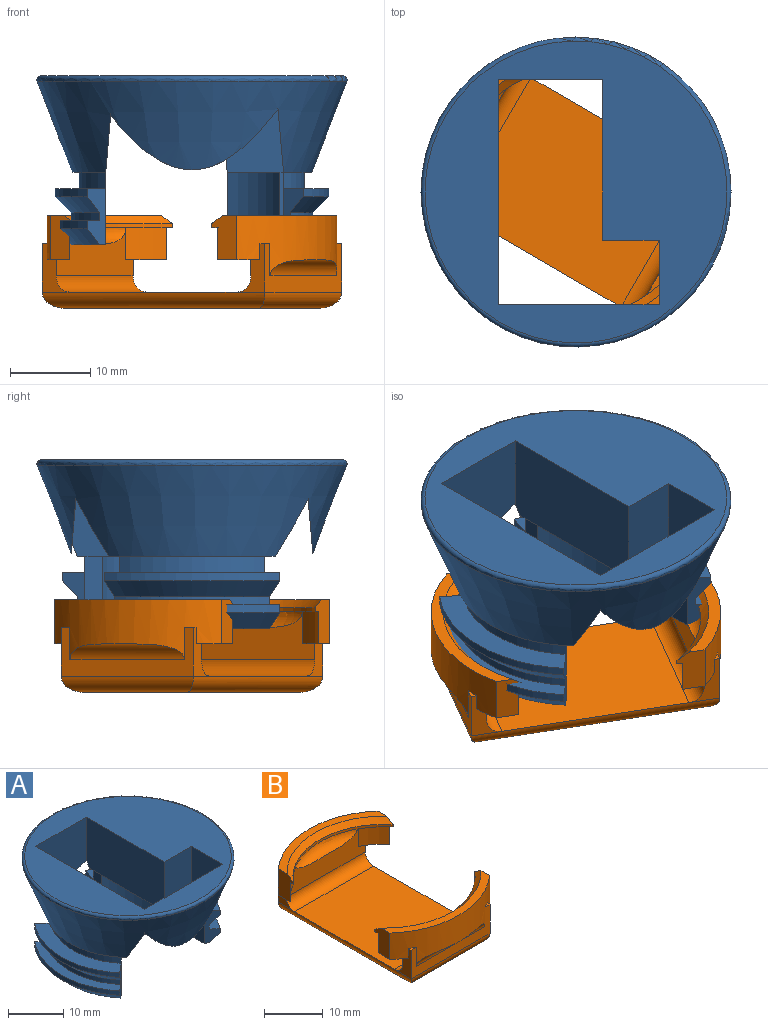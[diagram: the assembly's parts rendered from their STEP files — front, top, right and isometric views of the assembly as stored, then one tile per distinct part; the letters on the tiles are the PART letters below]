
ASSEMBLY  parts=2 mates=1
PART A: 42 faces, bbox 41.7x41.7x21 mm
  f0: cylinder r=15mm len=22.99mm, axis (0,0,1), area 28.1mm2, adj f25,f27,f32,f39
  f1: cylinder r=15mm len=19.28mm, axis (0,0,1), area 20.9mm2, adj f29,f30,f33,f37
  f2: plane 10.77x1.28mm, normal (0,0,-1), area 9.3mm2, adj f7,f23
  f3: plane 16.12x7.63mm, normal (0,0,-1), area 97.8mm2, adj f9,f10,f19
  f4: cone r=19.5mm half-angle=21deg, axis (0,0,1), area 1180.5mm2, adj f5,f6,f7,f8,f9,f11,f12,f14
  f5: plane 23.85x10.52mm, normal (0,0,-1), area 24.9mm2, adj f4,f9,f11,f16
  f6: plane 20.81x11.67mm, normal (0,1,-0.09), area 190.7mm2, adj f4,f7,f11,f13
  f7: plane 28.86x12mm, normal (1,0,-0.09), area 317.3mm2, adj f2,f4,f6,f8,f12,f13,f20,f22
  f8: plane 14.36x11.68mm, normal (0,-1,-0.09), area 136.9mm2, adj f4,f7,f9,f13
  f9: plane 20.92x12.01mm, normal (-1,0,-0.09), area 240.3mm2, adj f3,f4,f5,f8,f10,f13,f15
  f10: plane 12x8.05mm, normal (0,-1,-0.09), area 84.3mm2, adj f3,f9,f11,f13,f18
  f11: plane 12x9.42mm, normal (-1,0,-0.09), area 88.4mm2, adj f4,f5,f6,f10,f13,f17
  f12: plane 20.67x4.17mm, normal (0,0,-1), area 19mm2, adj f4,f7,f21
  f13: plane 37.52x37.52mm, normal (0,0,1), area 685.7mm2, adj f6,f7,f8,f9,f10,f11,f14
  f14: torus R=18.76mm, axis (0,0,1), area 118.2mm2, adj f4,f13
  f15: plane 9x2.12mm, normal (-1,0,0), area 19.1mm2, adj f9,f16,f19,f25,f35
  f16: cylinder r=14mm len=21.46mm, axis (0,0,1), area 52.5mm2, adj f5,f15,f17,f24
  f17: plane 9x3.21mm, normal (-1,0,0), area 28.9mm2, adj f11,f16,f18,f27,f35
  f18: plane 9x0.44mm, normal (0,-1,0), area 4mm2, adj f10,f17,f19,f35
  f19: cylinder r=12mm len=16.12mm, axis (0,0,1), area 175.3mm2, adj f3,f15,f18,f35
  f20: plane 9x3.62mm, normal (1,0,0), area 32.5mm2, adj f7,f21,f23,f30,f34
  f21: cylinder r=14mm len=18mm, axis (0,0,1), area 39.1mm2, adj f12,f20,f22,f28
  f22: plane 9x3.62mm, normal (1,0,0), area 32.5mm2, adj f7,f21,f23,f29,f34
  f23: cylinder r=12mm len=10.77mm, axis (0,0,1), area 100.5mm2, adj f2,f20,f22,f34
  f24: plane 26.06x12.63mm, normal (0,0,1), area 87.2mm2, adj f16,f25,f26,f27
  f25: plane 7x2.85mm, normal (-0.95,0.31,0), area 15mm2, adj f0,f15,f24,f26,f32,f35,f38,f39
  f26: cylinder r=17mm len=26.06mm, axis (0,0,1), area 31.9mm2, adj f24,f25,f27,f32
  f27: plane 7x2.44mm, normal (-0.58,-0.81,0), area 15mm2, adj f0,f17,f24,f26,f32,f35,f38,f39
  f28: plane 21.85x6.28mm, normal (0,0,1), area 64.9mm2, adj f21,f29,f30,f31
  f29: plane 7x2.3mm, normal (0.64,0.77,0), area 15mm2, adj f1,f22,f28,f31,f33,f34,f36,f37
  f30: plane 7x2.3mm, normal (0.64,-0.77,0), area 15mm2, adj f1,f20,f28,f31,f33,f34,f36,f37
  f31: cylinder r=17mm len=21.85mm, axis (0,0,1), area 23.7mm2, adj f28,f29,f30,f33
  f32: cone r=15mm half-angle=45deg, axis (0,0,1), area 84.9mm2, adj f0,f25,f26,f27
  f33: cone r=15mm half-angle=45deg, axis (0,0,1), area 63.2mm2, adj f1,f29,f30,f31
  f34: plane 19.28x4.28mm, normal (0,0,-1), area 51.3mm2, adj f20,f22,f23,f29,f30,f41
  f35: plane 22.99x10.63mm, normal (0,0,-1), area 72.3mm2, adj f15,f17,f18,f19,f25,f27,f40
  f36: cylinder r=17mm len=21.85mm, axis (0,0,-1), area 23.7mm2, adj f29,f30,f37,f41
  f37: plane 21.85x5.51mm, normal (0,0,1), area 44.7mm2, adj f1,f29,f30,f36
  f38: cylinder r=17mm len=26.06mm, axis (0,0,-1), area 31.9mm2, adj f25,f27,f39,f40
  f39: plane 26.06x12.31mm, normal (0,0,1), area 60mm2, adj f0,f25,f27,f38
  f40: cone r=15mm half-angle=45deg, axis (0,0,1), area 84.9mm2, adj f25,f27,f35,f38
  f41: cone r=15mm half-angle=45deg, axis (0,0,1), area 63.2mm2, adj f29,f30,f34,f36
PART B: 46 faces, bbox 25.6x36x11.5 mm
  f0: plane 6x4mm, normal (-1,0,0), area 10.3mm2, adj f20,f22,f27,f28,f30,f36,f44
  f1: plane 6x4mm, normal (1,0,0), area 10.3mm2, adj f4,f5,f9,f15,f16,f39,f45
  f2: cylinder r=16mm len=4.25mm, axis (0,0,-1), area 21.9mm2, adj f9,f12,f15,f17
  f3: cylinder r=16mm len=4.25mm, axis (0,0,-1), area 21.9mm2, adj f22,f24,f27,f32
  f4: plane 1.25x0.71mm, normal (0,0,1), area 0.4mm2, adj f1,f5,f16
  f5: plane 19x6mm, normal (0,-1,0), area 48mm2, adj f1,f4,f6,f8,f16,f37,f43
  f6: plane 1.25x0.71mm, normal (0,0,1), area 0.4mm2, adj f5,f8,f16
  f7: plane 6x4mm, normal (1,0,0), area 10.3mm2, adj f20,f21,f27,f28,f29,f39,f44
  f8: plane 6x4mm, normal (-1,0,0), area 10.3mm2, adj f5,f6,f9,f14,f16,f36,f45
  f9: plane 19x6mm, normal (0,1,0), area 73mm2, adj f1,f2,f8,f13,f14,f15,f42,f45
  f10: plane 24x6.68mm, normal (0,0,1), area 39.8mm2, adj f16,f17,f18,f34
  f11: cylinder r=15.5mm len=24mm, axis (0,0,-1), area 13.7mm2, adj f12,f17,f18,f34
  f12: plane 24x6.19mm, normal (0,0,-1), area 13.6mm2, adj f2,f11,f13,f17,f18,f42
  f13: cylinder r=16mm len=4.25mm, axis (0,0,-1), area 21.9mm2, adj f9,f12,f14,f18
  f14: plane 4.71x4.25mm, normal (0,0,-1), area 7.4mm2, adj f8,f9,f13,f16,f18
  f15: plane 4.71x4.25mm, normal (0,0,-1), area 7.4mm2, adj f1,f2,f9,f16,f17
  f16: cylinder r=18mm len=24mm, axis (0,0,-1), area 143.1mm2, adj f1,f4,f5,f6,f8,f10,f14,f15
  f17: plane 5.55x3.65mm, normal (1,0,0), area 16mm2, adj f2,f10,f11,f12,f15,f16,f34
  f18: plane 5.55x3.65mm, normal (-1,0,0), area 16mm2, adj f10,f11,f12,f13,f14,f16,f34
  f19: plane 24x19mm, normal (0,0,1), area 456mm2, adj f36,f39,f44,f45
  f20: cylinder r=18mm len=24mm, axis (0,0,-1), area 143.1mm2, adj f0,f7,f21,f22,f26,f28,f29,f30
  f21: plane 4.71x4.25mm, normal (0,0,-1), area 7.4mm2, adj f7,f20,f23,f27,f31
  f22: plane 4.71x4.25mm, normal (0,0,-1), area 7.4mm2, adj f0,f3,f20,f27,f32
  f23: cylinder r=16mm len=4.25mm, axis (0,0,-1), area 21.9mm2, adj f21,f24,f27,f31
  f24: plane 24x6.19mm, normal (0,0,-1), area 13.6mm2, adj f3,f23,f25,f31,f32,f41
  f25: cylinder r=15.5mm len=24mm, axis (0,0,-1), area 13.7mm2, adj f24,f31,f32,f35
  f26: plane 24x6.68mm, normal (0,0,1), area 39.8mm2, adj f20,f31,f32,f35
  f27: plane 19x6mm, normal (0,-1,0), area 73mm2, adj f0,f3,f7,f21,f22,f23,f41,f44
  f28: plane 19x6mm, normal (0,1,0), area 48mm2, adj f0,f7,f20,f29,f30,f38,f40
  f29: plane 1.25x0.71mm, normal (0,0,1), area 0.4mm2, adj f7,f20,f28
  f30: plane 1.25x0.71mm, normal (0,0,1), area 0.4mm2, adj f0,f20,f28
  f31: plane 5.55x3.65mm, normal (1,0,0), area 16mm2, adj f20,f21,f23,f24,f25,f26,f35
  f32: plane 5.55x3.65mm, normal (-1,0,0), area 16mm2, adj f3,f20,f22,f24,f25,f26,f35
  f33: plane 28x15mm, normal (0,0,-1), area 420mm2, adj f36,f37,f38,f39
  f34: cone r=15.5mm half-angle=45deg, axis (0,0,1), area 38.4mm2, adj f10,f11,f17,f18
  f35: cone r=15.5mm half-angle=45deg, axis (0,0,1), area 38.4mm2, adj f25,f26,f31,f32
  f36: cylinder r=2mm len=32mm, axis (0,1,0), area 96mm2, adj f0,f8,f19,f33,f37,f38
  f37: cylinder r=2mm len=19mm, axis (-1,0,0), area 55.1mm2, adj f5,f33,f36,f39
  f38: cylinder r=2mm len=19mm, axis (1,0,0), area 55.1mm2, adj f28,f33,f36,f39
  f39: cylinder r=2mm len=32mm, axis (0,-1,0), area 96mm2, adj f1,f7,f19,f33,f37,f38
  f40: cylinder r=2mm len=16.49mm, axis (-1,0,0), area 39.8mm2, adj f20,f28
  f41: torus R=14mm, axis (0,0,1), area 38mm2, adj f24,f27
  f42: torus R=14mm, axis (0,0,1), area 38mm2, adj f9,f12
  f43: cylinder r=2mm len=16.49mm, axis (1,0,0), area 39.8mm2, adj f5,f16
  f44: cylinder r=2mm len=19mm, axis (-1,0,0), area 59.7mm2, adj f0,f7,f19,f27
  f45: cylinder r=2mm len=19mm, axis (1,0,0), area 59.7mm2, adj f1,f8,f9,f19
PLACE A at identity fixed
PLACE B rot(axis=(0,0,-1),120.2deg) t=(0,0,-22.87)mm
MATE cylindrical B.f2 <-> A.f23  axis (0,0,-1) through (0,0,-20.87)mm
